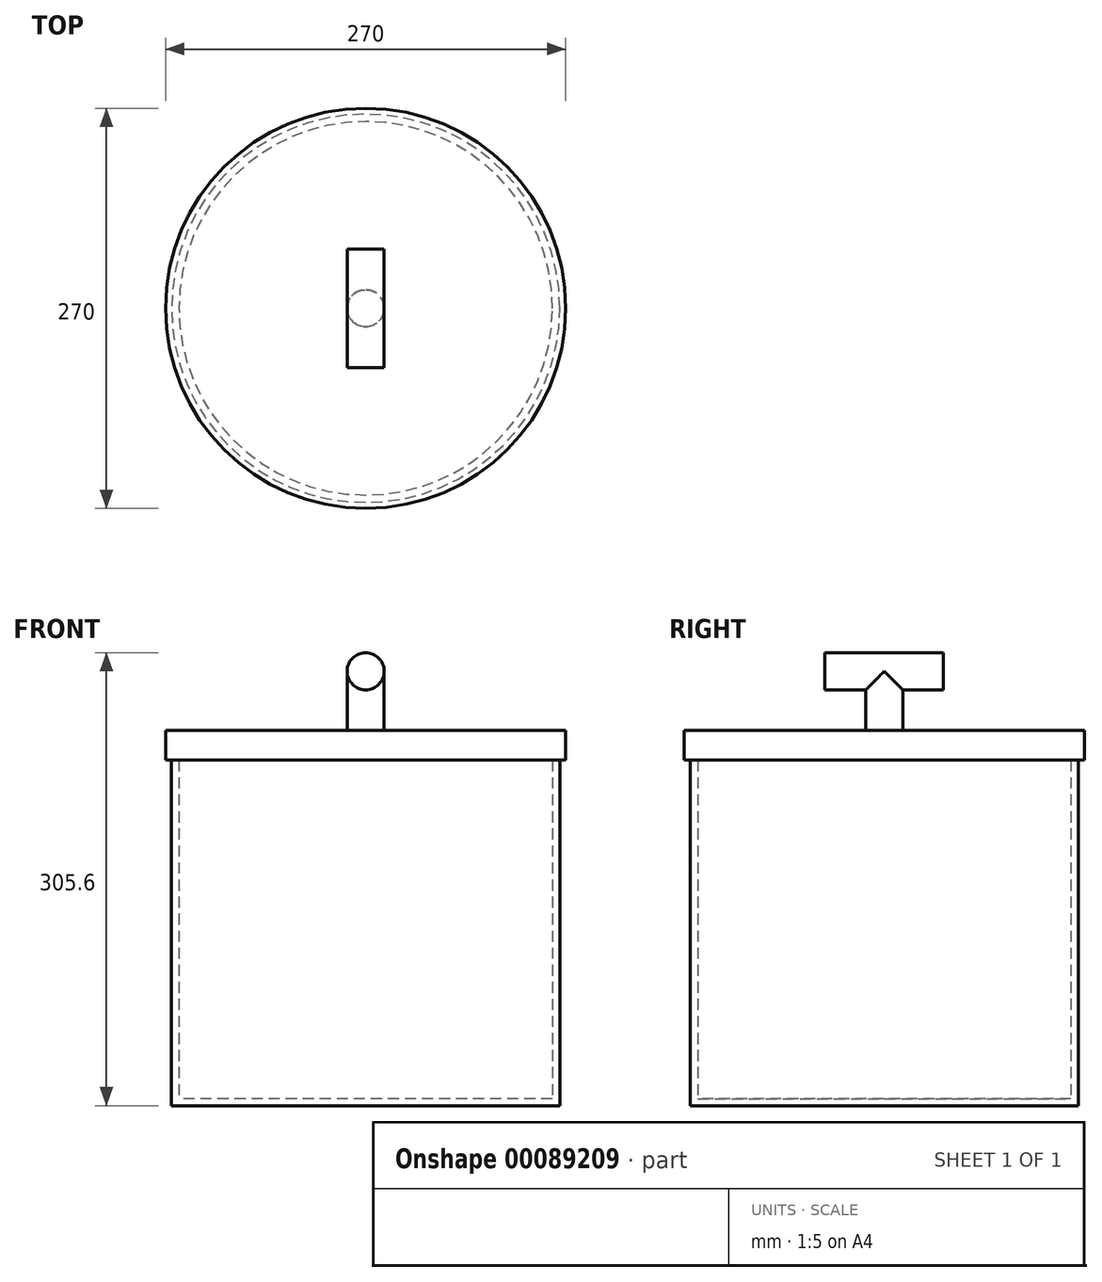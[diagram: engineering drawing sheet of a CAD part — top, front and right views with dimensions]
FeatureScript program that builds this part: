
annotation { "Feature Type Name" : "Feature", "Feature Type Description" : "" }
export const myFeature = defineFeature(function(context is Context, id is Id, definition is map)
    precondition{}
    {
        {
            var Q0;
            Q0=qCreatedBy(makeId("Top.planeOp"),FACE);
            var sketch = newSketch(context, id + "F0", { "sketchPlane" : qUnion([Q0])});
            skCircle(sketch, "E0", {"center": v(0, 0) * mm, "radius": 131 * mm});
            skCircle(sketch, "E1", {"center": v(0, 0) * mm, "radius": 127 * mm});
            skSolve(sketch);
        }
        {
            var Q0;
            Q0=makeQuery(id+"F0.imprint","IMPRINT",FACE,{"disambiguationData":[TD([[makeQuery(id+"F0.imprint","IMPRINT",EDGE,{"derivedFrom":sQuery(id+"F0.wireOp",EDGE,"E0")}),1.0]])]});
            var Q1;
            Q1=makeQuery(id+"F0.imprint","IMPRINT",FACE,{"disambiguationData":[TD([[makeQuery(id+"F0.imprint","IMPRINT",EDGE,{"derivedFrom":sQuery(id+"F0.wireOp",EDGE,"E1")}),1.0]])]});
            extrude(context, id + "F1", {"entities" : qUnion([Q0, Q1]), "oppositeDirection" : true, "depth" : 4.5 * mm});
        }
        {
            var Q0;
            Q0=makeQuery(id+"F1.opExtrude","CAP_FACE",FACE,{"disambiguationData":[OSD([sQuery(id+"F0.wireOp",EDGE,"E0")])],"isStart":true});
            var sketch = newSketch(context, id + "F2", { "sketchPlane" : qUnion([Q0])});
            skCircle(sketch, "E2", {"center": v(0, 0) * mm, "radius": 131 * mm});
            skCircle(sketch, "E3", {"center": v(0, 0) * mm, "radius": 126 * mm});
            skSolve(sketch);
        }
        {
            var Q0;
            Q0=makeQuery(id+"F2.imprint","IMPRINT",FACE,{"disambiguationData":[TD([[makeQuery(id+"F2.imprint","IMPRINT",EDGE,{"derivedFrom":sQuery(id+"F2.wireOp",EDGE,"E2")}),1.0]])]});
            extrude(context, id + "F3", {"entities" : qUnion([Q0]), "operationType" : NewBodyOperationType.ADD, "depth" : 228.6 * mm});
        }
        {
            var Q0;
            Q0=makeQuery(id+"F3.opExtrude","CAP_FACE",FACE,{"disambiguationData":[OSD([sQuery(id+"F2.wireOp",EDGE,"E2"),sQuery(id+"F2.wireOp",EDGE,"E3")])],"isStart":false});
            var sketch = newSketch(context, id + "F4", { "sketchPlane" : qUnion([Q0])});
            skCircle(sketch, "E4", {"center": v(0, 0) * mm, "radius": 135 * mm});
            skSolve(sketch);
        }
        {
            var Q0;
            Q0 = qSketchRegion(id + "F4", true);
            var Q1;
            Q1=makeQuery(id+"F4.imprint","IMPRINT",FACE,{"disambiguationData":[TD([[makeQuery(id+"F4.imprint","IMPRINT",EDGE,{"derivedFrom":makeQuery(id+"F3.opExtrude","CAP_EDGE",EDGE,{"disambiguationData":[OSD([sQuery(id+"F2.wireOp",EDGE,"E3")])],"isStart":false})}),1.0]])]});
            extrude(context, id + "F5", {"entities" : qUnion([Q0, Q1]), "operationType" : NewBodyOperationType.ADD, "depth" : 20 * mm});
        }
        {
            var Q0;
            Q0=makeQuery(id+"F5.opExtrude","CAP_FACE",FACE,{"disambiguationData":[OSD([sQuery(id+"F4.wireOp",EDGE,"E4")])],"isStart":false});
            var sketch = newSketch(context, id + "F6", { "sketchPlane" : qUnion([Q0])});
            skCircle(sketch, "E5", {"center": v(0, 0) * mm, "radius": 12.5 * mm});
            skSolve(sketch);
        }
        {
            var Q0;
            Q0=makeQuery(id+"F6.imprint","IMPRINT",FACE,{"disambiguationData":[TD([[makeQuery(id+"F6.imprint","IMPRINT",EDGE,{"derivedFrom":sQuery(id+"F6.wireOp",EDGE,"E5")}),1.0]])]});
            extrude(context, id + "F7", {"entities" : qUnion([Q0]), "operationType" : NewBodyOperationType.ADD, "depth" : 40 * mm});
        }
        {
            var Q0;
            Q0=qCreatedBy(makeId("Front.planeOp"),FACE);
            var sketch = newSketch(context, id + "F8", { "sketchPlane" : qUnion([Q0])});
            skCircle(sketch, "E6", {"center": v(0, 288.6) * mm, "radius": 12.5 * mm});
            skSolve(sketch);
        }
        {
            var Q0;
            Q0 = qSketchRegion(id + "F8", true);
            extrude(context, id + "F9", {"entities" : qUnion([Q0]), "operationType" : NewBodyOperationType.ADD, "oppositeDirection" : true, "depth" : 40 * mm, "hasSecondDirection" : true, "secondDirectionOppositeDirection" : false, "secondDirectionDepth" : 40 * mm});
        }
    });
